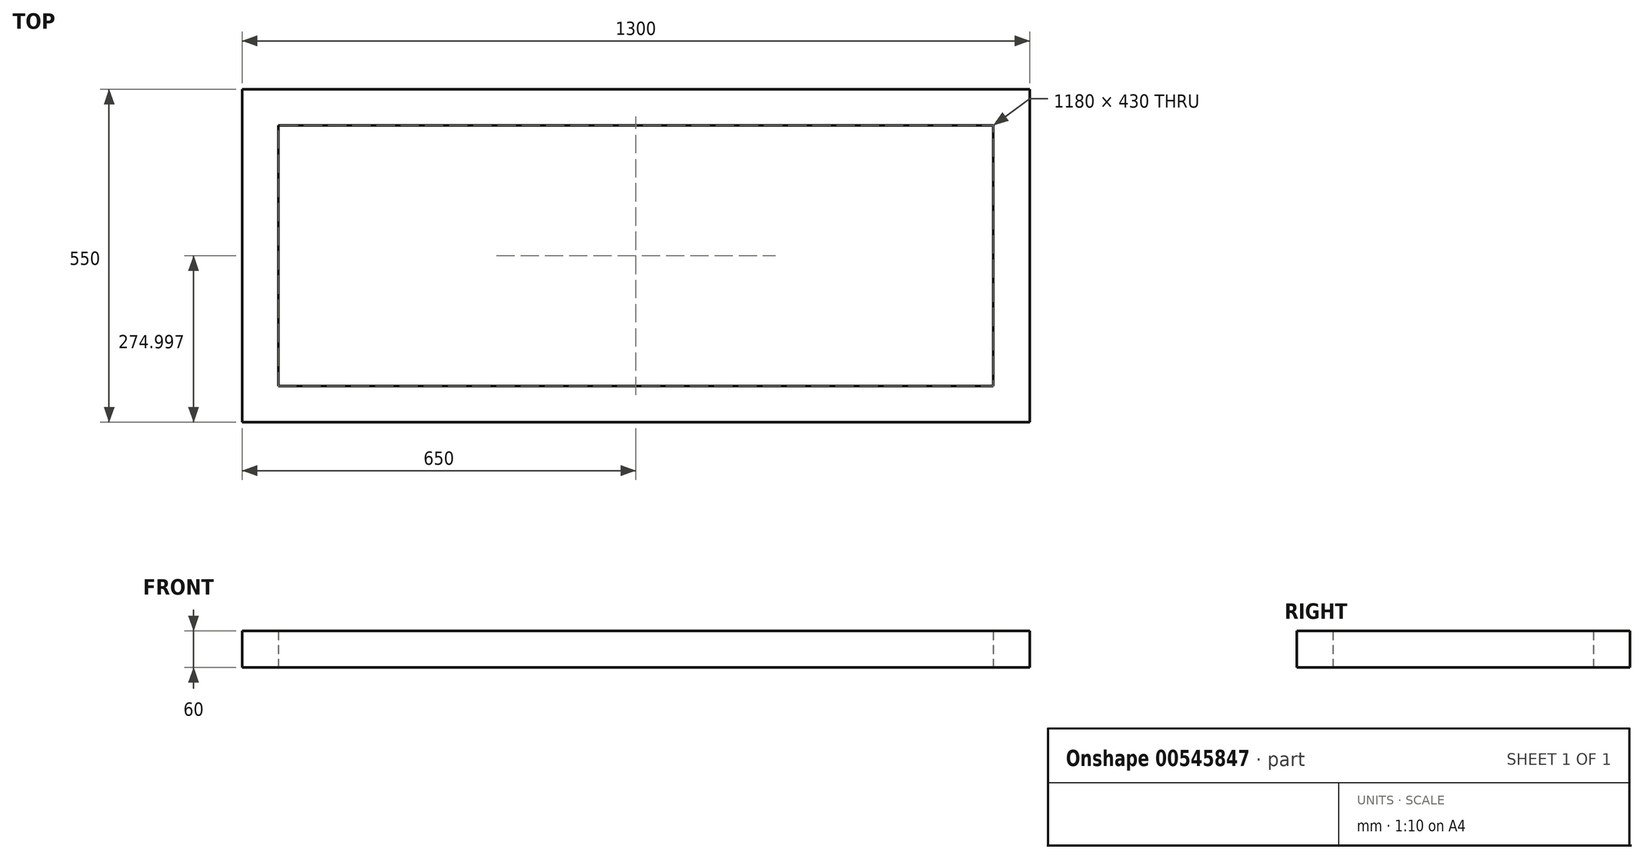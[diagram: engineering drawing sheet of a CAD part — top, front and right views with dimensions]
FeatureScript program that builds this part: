
annotation { "Feature Type Name" : "Feature", "Feature Type Description" : "" }
export const myFeature = defineFeature(function(context is Context, id is Id, definition is map)
    precondition{}
    {
        {
            var Q0;
            Q0=qCreatedBy(makeId("Top.planeOp"),FACE);
            var sketch = newSketch(context, id + "F0", { "sketchPlane" : qUnion([Q0])});
            skLineSegment(sketch, "E0.bottom", {"start": v(-650, 578.54) * mm, "end": v(650, 578.54) * mm});
            skLineSegment(sketch, "E0.top", {"start": v(-650, 28.54) * mm, "end": v(650, 28.54) * mm});
            skLineSegment(sketch, "E0.left", {"start": v(-650, 578.54) * mm, "end": v(-650, 28.54) * mm});
            skLineSegment(sketch, "E0.right", {"start": v(650, 578.54) * mm, "end": v(650, 28.54) * mm});
            skLineSegment(sketch, "E1.0", {"start": v(-590, 518.54) * mm, "end": v(590, 518.54) * mm});
            skLineSegment(sketch, "E1.1", {"start": v(-590, 518.54) * mm, "end": v(-590, 88.54) * mm});
            skLineSegment(sketch, "E1.2", {"start": v(-590, 88.54) * mm, "end": v(590, 88.54) * mm});
            skLineSegment(sketch, "E1.3", {"start": v(590, 518.54) * mm, "end": v(590, 88.54) * mm});
            skSolve(sketch);
        }
        {
            var Q0;
            Q0=makeQuery(id+"F0.imprint","IMPRINT",FACE,{"disambiguationData":[TD([[makeQuery(id+"F0.imprint","IMPRINT",EDGE,{"derivedFrom":sQuery(id+"F0.wireOp",EDGE,"E0.bottom")}),-1.0]])]});
            extrude(context, id + "F1", {"entities" : qUnion([Q0]), "endBound" : BoundingType.SYMMETRIC, "depth" : 60 * mm, "offsetDistance" : 25 * mm});
        }
    });
